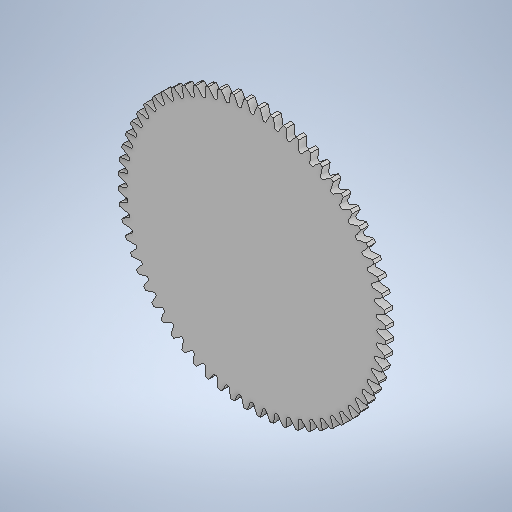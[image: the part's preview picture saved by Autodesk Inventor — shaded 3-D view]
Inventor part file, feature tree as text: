
AUTODESK INVENTOR PART (.ipt)
format: ipt  version: 2025 (Build 290162010, 162A)  size: 500,224 bytes
history: native  units: mm
features: extrude x2, pattern_circular x1
ambient origin geometry x8: Origin, YZ Plane, XZ Plane, XY Plane, X Axis, Y Axis, Z Axis, Center Point
bodies: Solid1 (feature_tree)
feature tree (3):
  extrude  "Extrusion1"  Depth=24.0mm TaperAngle=0.0deg
  extrude  "Extrusion2"  TaperAngle=0.0deg  [1 undecoded]
  pattern_circular  "Circular Pattern1"  Count=64 Angle=360.0deg
note: 1 required parameter value undecoded (feature->parameter linkage not recoverable at this tier; creation-order binding heuristic only, values carry confidence <= 0.55)
